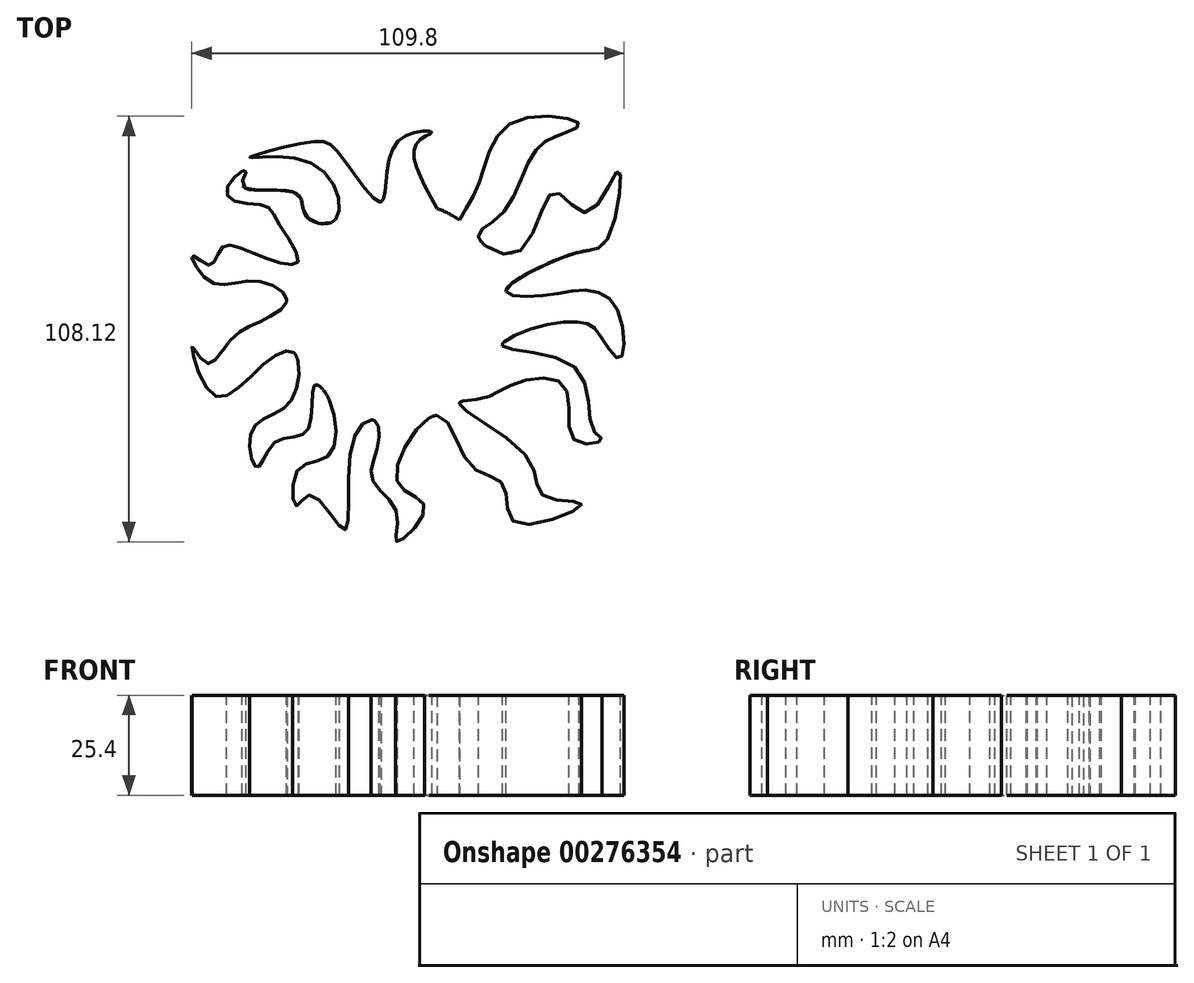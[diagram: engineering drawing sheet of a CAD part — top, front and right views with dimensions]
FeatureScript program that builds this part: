
annotation { "Feature Type Name" : "Feature", "Feature Type Description" : "" }
export const myFeature = defineFeature(function(context is Context, id is Id, definition is map)
    precondition{}
    {
        {
            var Q0;
            Q0=qCreatedBy(makeId("Top.planeOp"),FACE);
            var sketch = newSketch(context, id + "F0", { "sketchPlane" : qUnion([Q0])});
            skCircle(sketch, "E0", {"center": v(-15.82, 30.12) * mm, "radius": 28.2 * mm});
            skFitSpline(sketch, "E1", {"points": [v(0, 53.46) * mm, v(5.48, 64.2) * mm, v(14, 78.49) * mm, v(30.42, 77.88) * mm, v(26.47, 75.45) * mm, v(19.17, 70.88) * mm, v(10.65, 54.76) * mm, v(4.88, 49.27) * mm, v(14.9, 45.33) * mm, v(24.03, 60.54) * mm, v(32.55, 55.37) * mm, v(40.46, 66.02) * mm, v(37.72, 48.68) * mm, v(32.25, 45.63) * mm, v(22.2, 42.29) * mm, v(11.88, 35.43) * mm, v(19.77, 34.07) * mm, v(32.55, 35.6) * mm, v(40.46, 30.12) * mm, v(40.77, 18.25) * mm, v(35.6, 24.34) * mm, v(31.64, 27.38) * mm, v(18.56, 25.86) * mm, v(11.02, 21.47) * mm, v(29.5, 15.82) * mm, v(34.07, 0) * mm, v(36.2, -2.43) * mm, v(29.2, -2.43) * mm, v(26.77, 11.26) * mm, v(14, 11.86) * mm, v(6.08, 8.21) * mm, v(0, 6.77) * mm, v(17.64, -7.3) * mm, v(21.6, -16.73) * mm, v(31.03, -18.86) * mm, v(14.3, -23.42) * mm, v(11.26, -14) * mm, v(2.74, -8.7) * mm, v(-5.7, 3.8) * mm, v(-15.82, -12.91) * mm, v(-8.82, -19.47) * mm, v(-15.82, -28.3) * mm, v(-15.82, -21.3) * mm, v(-22.1, -12.45) * mm, v(-20.69, -3.65) * mm, v(-21.58, 2.51) * mm, v(-27.08, -2.74) * mm, v(-29.2, -25.25) * mm, v(-37.72, -16.43) * mm, v(-41.37, -19.17) * mm, v(-41.07, -10.04) * mm, v(-33.16, -6.39) * mm, v(-33.07, 7.81) * mm, v(-36.85, 11.33) * mm, v(-38.64, 0) * mm, v(-46.85, -3.04) * mm, v(-51.41, -9.43) * mm, v(-52.63, 0) * mm, v(-43.2, 7) * mm, v(-42.05, 19.76) * mm, v(-51.1, 15.52) * mm, v(-62.67, 9.13) * mm, v(-67.84, 21.3) * mm, v(-64.2, 17.04) * mm, v(-58.23, 22.84) * mm, v(-49.9, 27.99) * mm, v(-43.83, 33.38) * mm, v(-52.63, 38.03) * mm, v(-63.28, 37.72) * mm, v(-67.84, 44.42) * mm, v(-63.28, 41.98) * mm, v(-60.24, 46.55) * mm, v(-50.2, 44.11) * mm, v(-40.94, 42.94) * mm, v(-46.24, 53.24) * mm, v(-49.36, 57.07) * mm, v(-58.1, 58.71) * mm, v(-58.1, 63.28) * mm, v(-54.15, 66.02) * mm, v(-55.06, 62.06) * mm, v(-41.37, 60.24) * mm, v(-38.94, 54.46) * mm, v(-31.5, 53.56) * mm, v(-37.01, 67.57) * mm, v(-53.24, 69.36) * mm, v(-37.42, 73.32) * mm, v(-30.65, 70.51) * mm, v(-19.86, 58.03) * mm, v(-15.82, 73.15) * mm, v(-7, 75.75) * mm, v(-10.9, 72.86) * mm, v(-5.67, 56.43) * mm], "startDerivative": vector(500.53, 805.89) * mm, "endDerivative": vector(783.83, -1391.22) * mm});
            skPoint(sketch, "E2", {"position": v(-124.73, 21.9) * mm});
            skSolve(sketch);
        }
        {
            var Q0;
            {var subQ0=sQuery(id+"F0.wireOp",EDGE,"E1");var subQ1=sQuery(id+"F0.wireOp",EDGE,"E0");var subQ4=makeQuery(id+"F0.imprint","INTERSECT",VERTEX,{"disambiguationData":[OD(2.0)],"derivedFrom":[subQ1,subQ0]});Q0=makeQuery(id+"F0.imprint","IMPRINT",FACE,{"disambiguationData":[TD([[makeQuery(id+"F0.imprint","IMPRINT",EDGE,{"disambiguationData":[TD([[subQ4,-1.0]])],"derivedFrom":subQ1}),1.0]])]});}
            var Q1;
            {var subQ0=sQuery(id+"F0.wireOp",EDGE,"E1");var subQ1=sQuery(id+"F0.wireOp",EDGE,"E0");var subQ2=makeQuery(id+"F0.imprint","INTERSECT",VERTEX,{"disambiguationData":[OD(13.0)],"derivedFrom":[subQ1,subQ0]});Q1=makeQuery(id+"F0.imprint","IMPRINT",FACE,{"disambiguationData":[TD([[makeQuery(id+"F0.imprint","IMPRINT",EDGE,{"disambiguationData":[TD([[subQ2,-1.0]])],"derivedFrom":subQ1}),-1.0]])]});}
            var Q2;
            {var subQ0=sQuery(id+"F0.wireOp",EDGE,"E1");var subQ1=sQuery(id+"F0.wireOp",EDGE,"E0");var subQ2=makeQuery(id+"F0.imprint","INTERSECT",VERTEX,{"disambiguationData":[OD(15.0)],"derivedFrom":[subQ1,subQ0]});Q2=makeQuery(id+"F0.imprint","IMPRINT",FACE,{"disambiguationData":[TD([[makeQuery(id+"F0.imprint","IMPRINT",EDGE,{"disambiguationData":[TD([[subQ2,-1.0]])],"derivedFrom":subQ1}),-1.0]])]});}
            var Q3;
            {var subQ0=sQuery(id+"F0.wireOp",EDGE,"E1");var subQ1=sQuery(id+"F0.wireOp",EDGE,"E0");var subQ2=makeQuery(id+"F0.imprint","INTERSECT",VERTEX,{"disambiguationData":[OD(17.0)],"derivedFrom":[subQ1,subQ0]});Q3=makeQuery(id+"F0.imprint","IMPRINT",FACE,{"disambiguationData":[TD([[makeQuery(id+"F0.imprint","IMPRINT",EDGE,{"disambiguationData":[TD([[subQ2,-1.0]])],"derivedFrom":subQ1}),-1.0]])]});}
            var Q4;
            {var subQ0=sQuery(id+"F0.wireOp",EDGE,"E1");var subQ1=sQuery(id+"F0.wireOp",EDGE,"E0");var subQ2=makeQuery(id+"F0.imprint","INTERSECT",VERTEX,{"disambiguationData":[OD(21.0)],"derivedFrom":[subQ1,subQ0]});Q4=makeQuery(id+"F0.imprint","IMPRINT",FACE,{"disambiguationData":[TD([[makeQuery(id+"F0.imprint","IMPRINT",EDGE,{"disambiguationData":[TD([[subQ2,-1.0]])],"derivedFrom":subQ1}),-1.0]])]});}
            var Q5;
            {var subQ0=sQuery(id+"F0.wireOp",EDGE,"E1");var subQ1=sQuery(id+"F0.wireOp",EDGE,"E0");var subQ2=makeQuery(id+"F0.imprint","INTERSECT",VERTEX,{"disambiguationData":[OD(19.0)],"derivedFrom":[subQ1,subQ0]});Q5=makeQuery(id+"F0.imprint","IMPRINT",FACE,{"disambiguationData":[TD([[makeQuery(id+"F0.imprint","IMPRINT",EDGE,{"disambiguationData":[TD([[subQ2,-1.0]])],"derivedFrom":subQ1}),-1.0]])]});}
            var Q6;
            {var subQ0=sQuery(id+"F0.wireOp",EDGE,"E1");var subQ1=sQuery(id+"F0.wireOp",EDGE,"E0");var subQ2=makeQuery(id+"F0.imprint","INTERSECT",VERTEX,{"disambiguationData":[OD(3.0)],"derivedFrom":[subQ1,subQ0]});Q6=makeQuery(id+"F0.imprint","IMPRINT",FACE,{"disambiguationData":[TD([[makeQuery(id+"F0.imprint","IMPRINT",EDGE,{"disambiguationData":[TD([[subQ2,1.0]])],"derivedFrom":subQ1}),-1.0]])]});}
            var Q7;
            {var subQ0=sQuery(id+"F0.wireOp",EDGE,"E1");var subQ1=sQuery(id+"F0.wireOp",EDGE,"E0");var subQ2=makeQuery(id+"F0.imprint","INTERSECT",VERTEX,{"disambiguationData":[OD(23.0)],"derivedFrom":[subQ1,subQ0]});Q7=makeQuery(id+"F0.imprint","IMPRINT",FACE,{"disambiguationData":[TD([[makeQuery(id+"F0.imprint","IMPRINT",EDGE,{"disambiguationData":[TD([[subQ2,-1.0]])],"derivedFrom":subQ1}),-1.0]])]});}
            var Q8;
            {var subQ0=sQuery(id+"F0.wireOp",EDGE,"E1");var subQ1=sQuery(id+"F0.wireOp",EDGE,"E0");var subQ2=makeQuery(id+"F0.imprint","INTERSECT",VERTEX,{"disambiguationData":[OD(2.0)],"derivedFrom":[subQ1,subQ0]});Q8=makeQuery(id+"F0.imprint","IMPRINT",FACE,{"disambiguationData":[TD([[makeQuery(id+"F0.imprint","IMPRINT",EDGE,{"disambiguationData":[TD([[subQ2,-1.0]])],"derivedFrom":subQ1}),-1.0]])]});}
            var Q9;
            {var subQ0=sQuery(id+"F0.wireOp",EDGE,"E1");var subQ1=sQuery(id+"F0.wireOp",EDGE,"E0");var subQ2=makeQuery(id+"F0.imprint","INTERSECT",VERTEX,{"disambiguationData":[OD(0.0)],"derivedFrom":[subQ1,subQ0]});Q9=makeQuery(id+"F0.imprint","IMPRINT",FACE,{"disambiguationData":[TD([[makeQuery(id+"F0.imprint","IMPRINT",EDGE,{"disambiguationData":[TD([[subQ2,1.0]])],"derivedFrom":subQ1}),-1.0]])]});}
            var Q10;
            {var subQ0=sQuery(id+"F0.wireOp",EDGE,"E1");var subQ1=sQuery(id+"F0.wireOp",EDGE,"E0");var subQ2=makeQuery(id+"F0.imprint","INTERSECT",VERTEX,{"disambiguationData":[OD(1.0)],"derivedFrom":[subQ1,subQ0]});Q10=makeQuery(id+"F0.imprint","IMPRINT",FACE,{"disambiguationData":[TD([[makeQuery(id+"F0.imprint","IMPRINT",EDGE,{"disambiguationData":[TD([[subQ2,-1.0]])],"derivedFrom":subQ1}),-1.0]])]});}
            var Q11;
            {var subQ0=sQuery(id+"F0.wireOp",EDGE,"E1");var subQ1=sQuery(id+"F0.wireOp",EDGE,"E0");var subQ2=makeQuery(id+"F0.imprint","INTERSECT",VERTEX,{"disambiguationData":[OD(7.0)],"derivedFrom":[subQ1,subQ0]});Q11=makeQuery(id+"F0.imprint","IMPRINT",FACE,{"disambiguationData":[TD([[makeQuery(id+"F0.imprint","IMPRINT",EDGE,{"disambiguationData":[TD([[subQ2,-1.0]])],"derivedFrom":subQ1}),-1.0]])]});}
            var Q12;
            {var subQ0=sQuery(id+"F0.wireOp",EDGE,"E1");var subQ1=sQuery(id+"F0.wireOp",EDGE,"E0");var subQ2=makeQuery(id+"F0.imprint","INTERSECT",VERTEX,{"disambiguationData":[OD(9.0)],"derivedFrom":[subQ1,subQ0]});Q12=makeQuery(id+"F0.imprint","IMPRINT",FACE,{"disambiguationData":[TD([[makeQuery(id+"F0.imprint","IMPRINT",EDGE,{"disambiguationData":[TD([[subQ2,-1.0]])],"derivedFrom":subQ1}),-1.0]])]});}
            var Q13;
            {var subQ0=sQuery(id+"F0.wireOp",EDGE,"E1");var subQ1=sQuery(id+"F0.wireOp",EDGE,"E0");var subQ2=makeQuery(id+"F0.imprint","INTERSECT",VERTEX,{"disambiguationData":[OD(11.0)],"derivedFrom":[subQ1,subQ0]});Q13=makeQuery(id+"F0.imprint","IMPRINT",FACE,{"disambiguationData":[TD([[makeQuery(id+"F0.imprint","IMPRINT",EDGE,{"disambiguationData":[TD([[subQ2,-1.0]])],"derivedFrom":subQ1}),-1.0]])]});}
            extrude(context, id + "F1", {"entities" : qUnion([Q0, Q1, Q2, Q3, Q4, Q5, Q6, Q7, Q8, Q9, Q10, Q11, Q12, Q13]), "depth" : 25.4 * mm});
        }
    });
